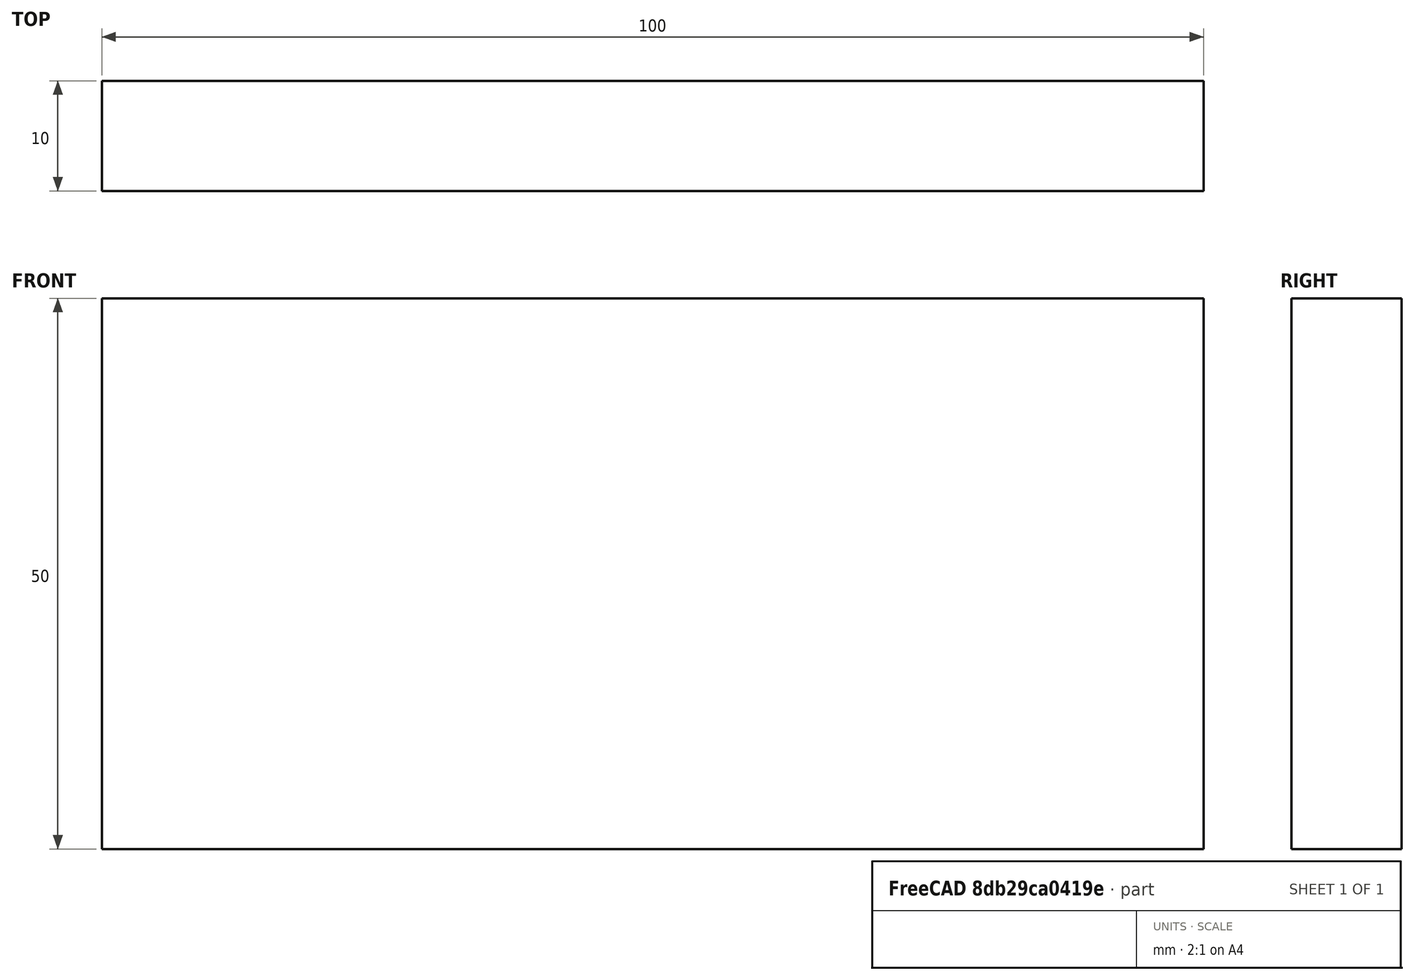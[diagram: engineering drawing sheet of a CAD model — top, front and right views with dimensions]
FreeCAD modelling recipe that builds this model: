
FCSTD DOCUMENT  (FreeCAD 0.15R4671 (Git))
Label: Flat Bar 100x10 EN10058 S235JR
License: All rights reserved
LicenseURL: http://en.wikipedia.org/wiki/All_rights_reserved
objects: Sketcher::SketchObject×1, Part::Extrusion×1
note: 2 computed .brp shape members not serialized (recipe doc carries the construction recipe); baked Part::Feature solids carry a one-line shape summary decoded from their .brp

FEATURE [Sketcher::SketchObject] Sketch
  sketch-geometry (4):
    g0: LineSegment StartX=-50 StartY=-5 StartZ=0 EndX=50 EndY=-5 EndZ=0
    g1: LineSegment StartX=50 StartY=-5 StartZ=0 EndX=50 EndY=5 EndZ=0
    g2: LineSegment StartX=50 StartY=5 StartZ=0 EndX=-50 EndY=5 EndZ=0
    g3: LineSegment StartX=-50 StartY=5 StartZ=0 EndX=-50 EndY=-5 EndZ=0
  constraints (12):
    c: Coincident(g0,g1)
    c: Coincident(g1,g2)
    c: Coincident(g2,g3)
    c: Coincident(g3,g0)
    c: Horizontal(g0)
    c: Horizontal(g2)
    c: Vertical(g1)
    c: Vertical(g3)
    c: Symmetric(g1,g2,g-2)
    c: Symmetric(g0,g1,g-1)
    c: DistanceY(g1) = 10
    c: DistanceX(g0) = 100
FEATURE [Part::Extrusion] Extrude  label="Flat Bar 100x10 EN10058 S235JR"
  Base = -> Sketch
  Dir = (0,0,50)
  Solid = true
